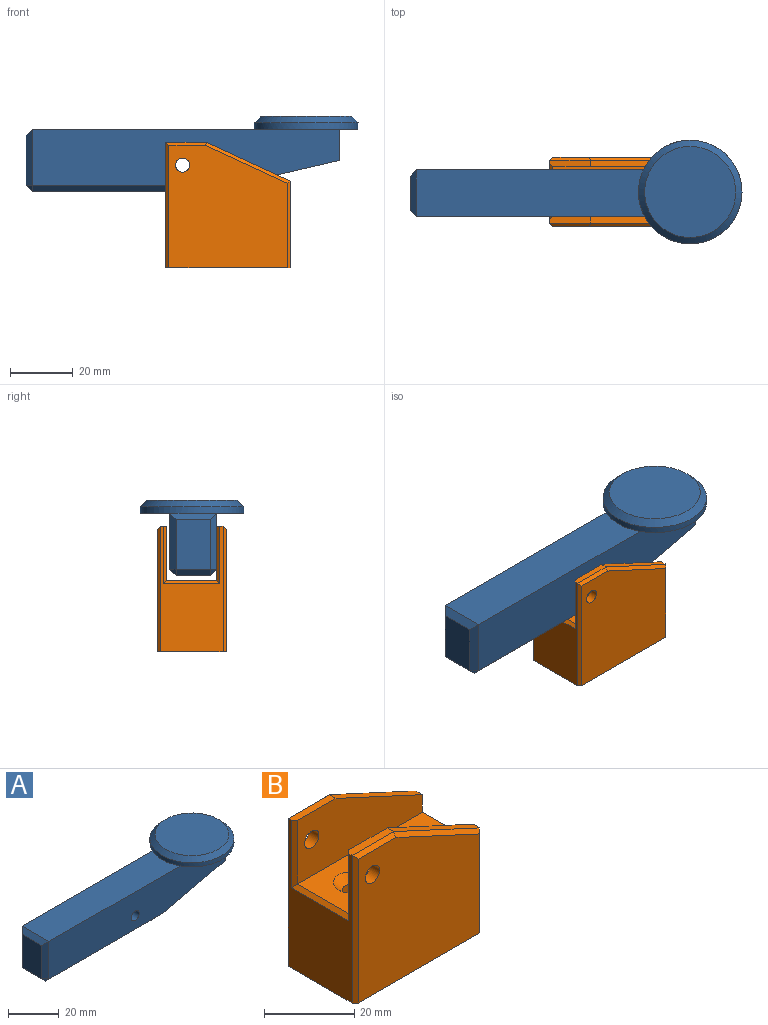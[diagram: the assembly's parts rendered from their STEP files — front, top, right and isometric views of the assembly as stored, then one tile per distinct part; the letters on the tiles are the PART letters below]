
ASSEMBLY  parts=2 mates=1
PART A: 22 faces, bbox 106x33.1x24 mm
  f0: plane 15x10mm, normal (1,0,0), area 150mm2, adj f1,f5,f7,f11
  f1: plane 98x18mm, normal (0,-1,0), area 1611.4mm2, adj f0,f2,f6,f7,f11,f19,f21
  f2: plane 72.96x15mm, normal (0,0,1), area 1073.1mm2, adj f1,f5,f8,f17
  f3: plane 16x11mm, normal (-1,0,0), area 176mm2, adj f15,f17,f18,f19
  f4: plane 55.28x11mm, normal (0,0,-1), area 608.1mm2, adj f11,f14,f18,f21
  f5: plane 98x18mm, normal (0,1,0), area 1611.4mm2, adj f0,f2,f6,f7,f11,f14,f15
  f6: cylinder r=2.25mm len=15mm, axis (0,1,0), area 212.1mm2, adj f1,f5
  f7: plane 33.09x31.49mm, normal (0,0,-1), area 463mm2, adj f0,f1,f5,f8
  f8: cylinder r=16.54mm len=33.09mm, axis (0,0,-1), area 207.9mm2, adj f2,f7,f10
  f9: plane 29.09x29.09mm, normal (0,0,1), area 664.6mm2, adj f10
  f10: cone r=14.54mm half-angle=45deg, axis (0,0,-1), area 276.3mm2, adj f8,f9
  f11: plane 42.72x15mm, normal (0.23,0,-0.97), area 555.1mm2, adj f0,f1,f4,f5,f13,f14,f21
  f12: plane 10.3x10.3mm, normal (0,0,-1), area 83.3mm2, adj f13
  f13: cylinder r=5.15mm len=10.3mm, axis (0,0,-1), area 227.7mm2, adj f11,f12
  f14: plane 63.82x2mm, normal (0,0.71,-0.71), area 168.4mm2, adj f4,f5,f11,f16
  f15: plane 18x2mm, normal (-0.71,0.71,0), area 48.1mm2, adj f3,f5,f16,f17
  f16: plane 2x2mm, normal (-0.58,0.58,-0.58), area 3.5mm2, adj f14,f15,f18
  f17: plane 15x2mm, normal (-0.71,0,0.71), area 36.8mm2, adj f2,f3,f15,f19
  f18: plane 11x2mm, normal (-0.71,0,-0.71), area 31.1mm2, adj f3,f4,f16,f20
  f19: plane 18x2mm, normal (-0.71,-0.71,0), area 48.1mm2, adj f1,f3,f17,f20
  f20: plane 2x2mm, normal (-0.58,-0.58,-0.58), area 3.5mm2, adj f18,f19,f21
  f21: plane 63.82x2mm, normal (0,-0.71,-0.71), area 168.4mm2, adj f1,f4,f11,f20
PART B: 30 faces, bbox 40x22x40 mm
  f0: plane 12.97x2mm, normal (0,0,1), area 25.4mm2, adj f3,f8,f16,f19,f21
  f1: plane 12.97x2mm, normal (0,0,1), area 25.4mm2, adj f3,f9,f15,f17,f24
  f2: plane 27.5x19.59mm, normal (1,0,0), area 462.6mm2, adj f8,f9,f10,f15,f16,f27,f28,f29
  f3: plane 40x20mm, normal (-1,0,0), area 471.5mm2, adj f0,f1,f17,f18,f19,f20,f23,f27
  f4: cylinder r=2.25mm len=4.5mm, axis (0,-1,0), area 42.4mm2, adj f6,f8
  f5: plane 39x38mm, normal (0,-1,0), area 1306.7mm2, adj f7,f23,f24,f25,f26,f27
  f6: plane 39x38mm, normal (0,1,0), area 1306.7mm2, adj f4,f20,f21,f22,f27,f29
  f7: cylinder r=2.25mm len=4.5mm, axis (0,-1,0), area 42.4mm2, adj f5,f9
  f8: plane 39x17.25mm, normal (0,-1,0), area 487.8mm2, adj f0,f2,f4,f10,f16,f19
  f9: plane 39x17.25mm, normal (0,1,0), area 487.8mm2, adj f1,f2,f7,f10,f15,f17
  f10: plane 39x16mm, normal (0,0,1), area 527.3mm2, adj f2,f8,f9,f13,f14,f18
  f11: cylinder r=1.74mm len=20.75mm, axis (0,0,1), area 227mm2, adj f13,f27
  f12: cylinder r=2.1mm len=20.75mm, axis (0,0,1), area 273.6mm2, adj f14,f27
  f13: cone r=1.74mm half-angle=45deg, axis (0,0,1), area 48.7mm2, adj f10,f11
  f14: cone r=2.1mm half-angle=45deg, axis (0,0,1), area 55.1mm2, adj f10,f12
  f15: plane 27.03x12.5mm, normal (0.42,0,0.91), area 59.5mm2, adj f1,f2,f9,f25,f28
  f16: plane 27.03x12.5mm, normal (0.42,0,0.91), area 59.6mm2, adj f0,f2,f8,f22
  f17: plane 18.25x1mm, normal (-0.71,0.71,0), area 25.1mm2, adj f1,f3,f9,f18
  f18: plane 18x1mm, normal (-0.71,0,0.71), area 24mm2, adj f3,f10,f17,f19
  f19: plane 18.25x1mm, normal (-0.71,-0.71,0), area 25.1mm2, adj f0,f3,f8,f18
  f20: plane 40x1mm, normal (-0.71,0.71,0), area 55.9mm2, adj f3,f6,f21,f27
  f21: plane 12.97x1mm, normal (0,0.71,0.71), area 17.5mm2, adj f0,f6,f20,f22
  f22: plane 27.25x13.14mm, normal (0.3,0.71,0.64), area 41.5mm2, adj f6,f16,f21,f29
  f23: plane 40x1mm, normal (-0.71,-0.71,0), area 55.9mm2, adj f3,f5,f24,f27
  f24: plane 12.97x1mm, normal (0,-0.71,0.71), area 17.5mm2, adj f1,f5,f23,f25
  f25: plane 27.08x13.14mm, normal (0.3,-0.71,0.64), area 41.5mm2, adj f5,f15,f24,f26,f28
  f26: plane 27.31x0.71mm, normal (0.71,-0.71,0), area 27.1mm2, adj f5,f25,f27,f28
  f27: plane 40x22mm, normal (0,0,-1), area 854.6mm2, adj f2,f3,f5,f6,f11,f12,f20,f23
  f28: plane 27.58x0.71mm, normal (0.92,-0.38,0), area 21mm2, adj f2,f15,f25,f26,f27
  f29: plane 27.5x1mm, normal (0.71,0.71,0), area 38.4mm2, adj f2,f6,f22,f27
PLACE A t=(-14.62,-4,5.23)mm
PLACE B at identity
MATE revolute A.f6 <-> B.f4  axis (0,-1,0) through (-14.62,-19,3.7)mm
